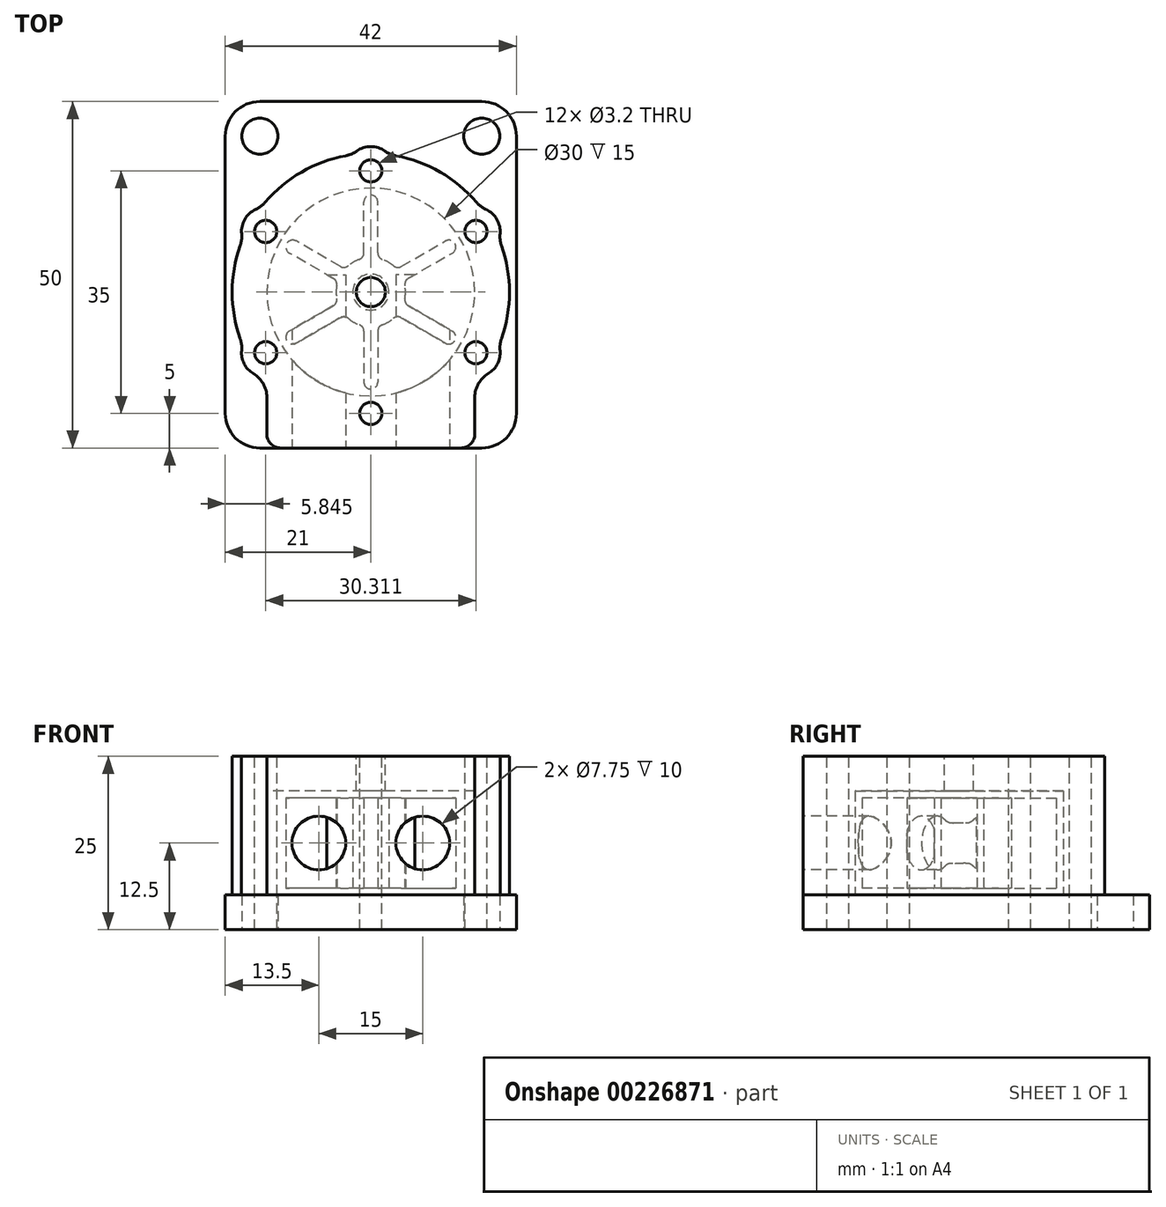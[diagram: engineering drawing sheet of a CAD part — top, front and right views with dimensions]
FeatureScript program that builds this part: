
annotation { "Feature Type Name" : "Feature", "Feature Type Description" : "" }
export const myFeature = defineFeature(function(context is Context, id is Id, definition is map)
    precondition{}
    {
        {
            var Q0;
            Q0=qCreatedBy(makeId("Top.planeOp"),FACE);
            var sketch = newSketch(context, id + "F0", { "sketchPlane" : qUnion([Q0])});
            skLineSegment(sketch, "E0.top", {"start": v(16, 27.5) * mm, "end": v(-16, 27.5) * mm});
            skLineSegment(sketch, "E0.left", {"start": v(21, -17.5) * mm, "end": v(21, 22.5) * mm});
            skLineSegment(sketch, "E0.right", {"start": v(-21, -17.5) * mm, "end": v(-21, 22.5) * mm});
            skPoint(sketch, "E0.middle", {"position": v(0, 0) * mm});
            skPoint(sketch, "E1.visualSharp", {"position": v(-21, 27.5) * mm});
            skArc(sketch, "E1.filletArc", {"start": v(-16, 27.5) * mm, "mid": v(-19.54, 26.04) * mm, "end": v(-21, 22.5) * mm});
            skPoint(sketch, "E2.visualSharp", {"position": v(21, 27.5) * mm});
            skArc(sketch, "E2.filletArc", {"start": v(21, 22.5) * mm, "mid": v(19.54, 26.04) * mm, "end": v(16, 27.5) * mm});
            skCircle(sketch, "E3", {"center": v(-16, 22.5) * mm, "radius": 2.6 * mm});
            skCircle(sketch, "E4", {"center": v(16, 22.5) * mm, "radius": 2.6 * mm});
            skLineSegment(sketch, "E5", {"start": v(-16, -22.5) * mm, "end": v(16, -22.5) * mm});
            skPoint(sketch, "E6.visualSharp", {"position": v(-21, -22.5) * mm});
            skArc(sketch, "E6.filletArc", {"start": v(-21, -17.5) * mm, "mid": v(-19.54, -21.04) * mm, "end": v(-16, -22.5) * mm});
            skPoint(sketch, "E7.visualSharp", {"position": v(21, -22.5) * mm});
            skArc(sketch, "E7.filletArc", {"start": v(16, -22.5) * mm, "mid": v(19.54, -21.04) * mm, "end": v(21, -17.5) * mm});
            skSolve(sketch);
        }
        {
            var Q0;
            Q0 = qSketchRegion(id + "F0", true);
            extrude(context, id + "F1", {"entities" : qUnion([Q0]), "depth" : 5 * mm});
        }
        {
            var Q0;
            Q0=makeQuery(id+"F1.opExtrude","CAP_FACE",FACE,{"disambiguationData":[OSD([sQuery(id+"F0.wireOp",EDGE,"E0.bottom"),sQuery(id+"F0.wireOp",EDGE,"E0.top"),sQuery(id+"F0.wireOp",EDGE,"E0.left"),sQuery(id+"F0.wireOp",EDGE,"E0.right"),sQuery(id+"F0.wireOp",EDGE,"E1.filletArc"),sQuery(id+"F0.wireOp",EDGE,"E2.filletArc"),sQuery(id+"F0.wireOp",EDGE,"c15cc097-3fda-4827-8514-8160edc4b4ba.filletArc"),sQuery(id+"F0.wireOp",EDGE,"696a4059-26aa-422c-bf07-b0a4ac1ae079.filletArc"),sQuery(id+"F0.wireOp",EDGE,"E3"),sQuery(id+"F0.wireOp",EDGE,"E4"),sQuery(id+"F0.wireOp",EDGE,"jZ877vgV-FuZ0-r36g-jPSG-0nmLSFL3s8fu"),sQuery(id+"F0.wireOp",EDGE,"1KYRIAWv-B9v9-mcC8-4xqL-udh9nFA10wgL")])],"isStart":false});
            var sketch = newSketch(context, id + "F2", { "sketchPlane" : qUnion([Q0])});
            skArc(sketch, "E8", {"start": v(18.85, -6.68) * mm, "mid": v(20, 0) * mm, "end": v(18.85, 6.68) * mm});
            skCircle(sketch, "E9", {"center": v(0, 0) * mm, "radius": 15 * mm});
            skLineSegment(sketch, "E10.left", {"start": v(15, -20.5) * mm, "end": v(15, -15.19) * mm});
            skLineSegment(sketch, "E10.right", {"start": v(-15, -20.5) * mm, "end": v(-15, -15.19) * mm});
            skPoint(sketch, "E10.middle", {"position": v(0, -7.67) * mm});
            skPoint(sketch, "E11.orphan", {"position": v(15, 12.15) * mm});
            skPoint(sketch, "E12.trimOffspring.end.orphan", {"position": v(-15, 12.15) * mm});
            skPoint(sketch, "E13.visualSharp", {"position": v(-15, -13.23) * mm});
            skPoint(sketch, "E14.visualSharp", {"position": v(15, -13.23) * mm});
            skLineSegment(sketch, "E15", {"start": v(-13, -22.5) * mm, "end": v(13, -22.5) * mm});
            skPoint(sketch, "E16.visualSharp", {"position": v(-15, -22.5) * mm});
            skArc(sketch, "E16.filletArc", {"start": v(-15, -20.5) * mm, "mid": v(-14.41, -21.91) * mm, "end": v(-13, -22.5) * mm});
            skPoint(sketch, "E17.visualSharp", {"position": v(15, -22.5) * mm});
            skArc(sketch, "E17.filletArc", {"start": v(13, -22.5) * mm, "mid": v(14.41, -21.91) * mm, "end": v(15, -20.5) * mm});
            skCircle(sketch, "E18", {"center": v(0, 0) * mm, "radius": 17.5 * mm, "construction": true});
            skArc(sketch, "E19", {"start": v(2.04, 20.35) * mm, "mid": v(0, 21) * mm, "end": v(-2.04, 20.35) * mm});
            skArc(sketch, "E20.trimOffspring", {"start": v(-3.64, 19.67) * mm, "mid": v(-10, 17.32) * mm, "end": v(-15.21, 12.98) * mm});
            skPoint(sketch, "E21.visualSharp", {"position": v(2.61, 19.83) * mm});
            skArc(sketch, "E21.filletArc", {"start": v(2.04, 20.35) * mm, "mid": v(2.8, 19.92) * mm, "end": v(3.64, 19.67) * mm});
            skPoint(sketch, "E22.visualSharp", {"position": v(-2.61, 19.83) * mm});
            skArc(sketch, "E22.filletArc", {"start": v(-3.64, 19.67) * mm, "mid": v(-2.8, 19.92) * mm, "end": v(-2.04, 20.35) * mm});
            skPoint(sketch, "E23.1.0", {"position": v(-15.87, 12.18) * mm});
            skPoint(sketch, "E23.1.1", {"position": v(-18.48, 7.65) * mm});
            skArc(sketch, "E23.1.2", {"start": v(-16.6, 11.94) * mm, "mid": v(-18.19, 10.5) * mm, "end": v(-18.64, 8.4) * mm});
            skArc(sketch, "E23.1.3", {"start": v(-18.85, 6.68) * mm, "mid": v(-18.65, 7.54) * mm, "end": v(-18.64, 8.4) * mm});
            skArc(sketch, "E23.1.4", {"start": v(-16.6, 11.94) * mm, "mid": v(-15.85, 12.38) * mm, "end": v(-15.21, 12.98) * mm});
            skPoint(sketch, "E23.2.0", {"position": v(-18.48, -7.65) * mm});
            skPoint(sketch, "E23.2.1", {"position": v(-15.87, -12.18) * mm});
            skArc(sketch, "E23.2.2", {"start": v(-18.64, -8.4) * mm, "mid": v(-18.28, -10.33) * mm, "end": v(-16.95, -11.76) * mm});
            skArc(sketch, "E23.2.4", {"start": v(-18.64, -8.4) * mm, "mid": v(-18.65, -7.54) * mm, "end": v(-18.85, -6.68) * mm});
            skPoint(sketch, "E23.3.0", {"position": v(-2.61, -19.83) * mm});
            skPoint(sketch, "E23.3.1", {"position": v(2.61, -19.83) * mm});
            skArc(sketch, "E23.3.2", {"start": v(-2.04, -20.35) * mm, "mid": v(0, -21) * mm, "end": v(2.04, -20.35) * mm});
            skArc(sketch, "E23.3.3", {"start": v(3.64, -19.67) * mm, "mid": v(2.8, -19.92) * mm, "end": v(2.04, -20.35) * mm});
            skArc(sketch, "E23.3.4", {"start": v(-2.04, -20.35) * mm, "mid": v(-2.8, -19.92) * mm, "end": v(-3.64, -19.67) * mm});
            skPoint(sketch, "E23.4.0", {"position": v(15.87, -12.18) * mm});
            skPoint(sketch, "E23.4.1", {"position": v(18.48, -7.65) * mm});
            skArc(sketch, "E23.4.2", {"start": v(16.95, -11.76) * mm, "mid": v(18.28, -10.33) * mm, "end": v(18.64, -8.4) * mm});
            skArc(sketch, "E23.4.3", {"start": v(18.85, -6.68) * mm, "mid": v(18.65, -7.54) * mm, "end": v(18.64, -8.4) * mm});
            skPoint(sketch, "E23.5.0", {"position": v(18.48, 7.65) * mm});
            skPoint(sketch, "E23.5.1", {"position": v(15.87, 12.18) * mm});
            skArc(sketch, "E23.5.2", {"start": v(18.64, 8.4) * mm, "mid": v(18.19, 10.5) * mm, "end": v(16.6, 11.94) * mm});
            skArc(sketch, "E23.5.3", {"start": v(15.21, 12.98) * mm, "mid": v(15.85, 12.38) * mm, "end": v(16.6, 11.94) * mm});
            skArc(sketch, "E23.5.4", {"start": v(18.64, 8.4) * mm, "mid": v(18.65, 7.54) * mm, "end": v(18.85, 6.68) * mm});
            skArc(sketch, "E24.trimOffspring", {"start": v(15.21, 12.98) * mm, "mid": v(10, 17.32) * mm, "end": v(3.64, 19.67) * mm});
            skArc(sketch, "E25.trimOffspring", {"start": v(-18.85, 6.68) * mm, "mid": v(-20, 0) * mm, "end": v(-18.85, -6.68) * mm});
            skPoint(sketch, "E26.newPointA", {"position": v(-16.6, -11.94) * mm});
            skArc(sketch, "E26.filletArc", {"start": v(-15, -15.19) * mm, "mid": v(-15.52, -13.22) * mm, "end": v(-16.95, -11.76) * mm});
            skPoint(sketch, "E27.newPointA", {"position": v(16.6, -11.94) * mm});
            skArc(sketch, "E27.filletArc", {"start": v(16.95, -11.76) * mm, "mid": v(15.52, -13.22) * mm, "end": v(15, -15.19) * mm});
            skSolve(sketch);
        }
        {
            var Q0;
            Q0=makeQuery(id+"F2.imprint","IMPRINT",FACE,{"disambiguationData":[TD([[makeQuery(id+"F2.imprint","IMPRINT",EDGE,{"derivedFrom":sQuery(id+"F2.wireOp",EDGE,"E8")}),1.0]])]});
            extrude(context, id + "F3", {"entities" : qUnion([Q0]), "depth" : 15 * mm});
        }
        {
            var Q0;
            Q0=makeQuery(id+"F3.opExtrude","CAP_FACE",FACE,{"disambiguationData":[OSD([sQuery(id+"F2.wireOp",EDGE,"E8"),sQuery(id+"F2.wireOp",EDGE,"E9"),sQuery(id+"F2.wireOp",EDGE,"E10.left"),sQuery(id+"F2.wireOp",EDGE,"E10.right"),sQuery(id+"F2.wireOp",EDGE,"E13.filletArc"),sQuery(id+"F2.wireOp",EDGE,"E14.filletArc"),sQuery(id+"F2.wireOp",EDGE,"E15"),sQuery(id+"F2.wireOp",EDGE,"E16.filletArc"),sQuery(id+"F2.wireOp",EDGE,"E17.filletArc")])],"isStart":false});
            var sketch = newSketch(context, id + "F4", { "sketchPlane" : qUnion([Q0])});
            skCircle(sketch, "E28", {"center": v(0, 0) * mm, "radius": 17.5 * mm, "construction": true});
            skLineSegment(sketch, "E29", {"start": v(0, 0) * mm, "end": v(0, 17.5) * mm, "construction": true});
            skCircle(sketch, "E30", {"center": v(0, 17.5) * mm, "radius": 1.6 * mm});
            skCircle(sketch, "E31.1.0", {"center": v(-15.16, 8.75) * mm, "radius": 1.6 * mm});
            skCircle(sketch, "E31.2.0", {"center": v(-15.16, -8.75) * mm, "radius": 1.6 * mm});
            skCircle(sketch, "E31.3.0", {"center": v(0, -17.5) * mm, "radius": 1.6 * mm});
            skCircle(sketch, "E31.4.0", {"center": v(15.16, -8.75) * mm, "radius": 1.6 * mm});
            skCircle(sketch, "E31.5.0", {"center": v(15.16, 8.75) * mm, "radius": 1.6 * mm});
            skLineSegment(sketch, "E32", {"start": v(-11, -18.5) * mm, "end": v(11, -18.5) * mm, "construction": true});
            skSolve(sketch);
        }
        {
            var Q0;
            Q0 = qSketchRegion(id + "F4", true);
            extrude(context, id + "F5", {"entities" : qUnion([Q0]), "operationType" : NewBodyOperationType.REMOVE, "oppositeDirection" : true, "depth" : 25 * mm});
        }
        {
            var Q0;
            Q0=makeQuery(id+"F3.opExtrude","CAP_FACE",FACE,{"disambiguationData":[OSD([sQuery(id+"F2.wireOp",EDGE,"E8"),sQuery(id+"F2.wireOp",EDGE,"E9"),sQuery(id+"F2.wireOp",EDGE,"E10.left"),sQuery(id+"F2.wireOp",EDGE,"E10.right"),sQuery(id+"F2.wireOp",EDGE,"E13.filletArc"),sQuery(id+"F2.wireOp",EDGE,"E14.filletArc"),sQuery(id+"F2.wireOp",EDGE,"E15"),sQuery(id+"F2.wireOp",EDGE,"E16.filletArc"),sQuery(id+"F2.wireOp",EDGE,"E17.filletArc")])],"isStart":false});
            var sketch = newSketch(context, id + "F6", { "sketchPlane" : qUnion([Q0])});
            skCircle(sketch, "E33.0", {"center": v(0, 0) * mm, "radius": 15 * mm, "construction": true});
            skCircle(sketch, "E34.0", {"center": v(0, 17.5) * mm, "radius": 1.6 * mm, "construction": true});
            skCircle(sketch, "E35.0", {"center": v(15.16, 8.75) * mm, "radius": 1.6 * mm, "construction": true});
            skCircle(sketch, "E36.0", {"center": v(15.16, -8.75) * mm, "radius": 1.6 * mm, "construction": true});
            skCircle(sketch, "E37.0", {"center": v(-15.16, -8.75) * mm, "radius": 1.6 * mm, "construction": true});
            skCircle(sketch, "E38.0", {"center": v(-15.16, 8.75) * mm, "radius": 1.6 * mm, "construction": true});
            skLineSegment(sketch, "E39.0.0", {"start": v(-15, -15.19) * mm, "end": v(-15, -20.5) * mm});
            skArc(sketch, "E39.0.1", {"start": v(-15, -20.5) * mm, "mid": v(-14.41, -21.91) * mm, "end": v(-13, -22.5) * mm});
            skLineSegment(sketch, "E39.0.2", {"start": v(-13, -22.5) * mm, "end": v(13, -22.5) * mm});
            skArc(sketch, "E39.0.3", {"start": v(13, -22.5) * mm, "mid": v(14.41, -21.91) * mm, "end": v(15, -20.5) * mm});
            skLineSegment(sketch, "E39.0.4", {"start": v(15, -20.5) * mm, "end": v(15, -15.19) * mm});
            skArc(sketch, "E39.0.5", {"start": v(15, -15.19) * mm, "mid": v(15.52, -13.22) * mm, "end": v(16.95, -11.76) * mm});
            skArc(sketch, "E39.0.6", {"start": v(16.95, -11.76) * mm, "mid": v(18.28, -10.33) * mm, "end": v(18.64, -8.4) * mm});
            skArc(sketch, "E39.0.7", {"start": v(18.64, -8.4) * mm, "mid": v(18.65, -7.54) * mm, "end": v(18.85, -6.68) * mm});
            skArc(sketch, "E39.0.8", {"start": v(18.85, -6.68) * mm, "mid": v(20, 0) * mm, "end": v(18.85, 6.68) * mm});
            skArc(sketch, "E39.0.9", {"start": v(18.85, 6.68) * mm, "mid": v(18.65, 7.54) * mm, "end": v(18.64, 8.4) * mm});
            skArc(sketch, "E39.0.10", {"start": v(18.64, 8.4) * mm, "mid": v(18.19, 10.5) * mm, "end": v(16.6, 11.94) * mm});
            skArc(sketch, "E39.0.11", {"start": v(16.6, 11.94) * mm, "mid": v(15.85, 12.38) * mm, "end": v(15.21, 12.98) * mm});
            skArc(sketch, "E39.0.12", {"start": v(15.21, 12.98) * mm, "mid": v(10, 17.32) * mm, "end": v(3.64, 19.67) * mm});
            skArc(sketch, "E39.0.13", {"start": v(3.64, 19.67) * mm, "mid": v(2.8, 19.92) * mm, "end": v(2.04, 20.35) * mm});
            skArc(sketch, "E39.0.14", {"start": v(2.04, 20.35) * mm, "mid": v(0, 21) * mm, "end": v(-2.04, 20.35) * mm});
            skArc(sketch, "E39.0.15", {"start": v(-2.04, 20.35) * mm, "mid": v(-2.8, 19.92) * mm, "end": v(-3.64, 19.67) * mm});
            skArc(sketch, "E39.0.16", {"start": v(-3.64, 19.67) * mm, "mid": v(-10, 17.32) * mm, "end": v(-15.21, 12.98) * mm});
            skArc(sketch, "E39.0.17", {"start": v(-15.21, 12.98) * mm, "mid": v(-15.85, 12.38) * mm, "end": v(-16.6, 11.94) * mm});
            skArc(sketch, "E39.0.18", {"start": v(-16.6, 11.94) * mm, "mid": v(-18.19, 10.5) * mm, "end": v(-18.64, 8.4) * mm});
            skArc(sketch, "E39.0.19", {"start": v(-18.64, 8.4) * mm, "mid": v(-18.65, 7.54) * mm, "end": v(-18.85, 6.68) * mm});
            skArc(sketch, "E39.0.20", {"start": v(-18.85, 6.68) * mm, "mid": v(-20, 0) * mm, "end": v(-18.85, -6.68) * mm});
            skArc(sketch, "E39.0.21", {"start": v(-18.85, -6.68) * mm, "mid": v(-18.65, -7.54) * mm, "end": v(-18.64, -8.4) * mm});
            skArc(sketch, "E39.0.22", {"start": v(-18.64, -8.4) * mm, "mid": v(-18.28, -10.33) * mm, "end": v(-16.95, -11.76) * mm});
            skArc(sketch, "E39.0.23", {"start": v(-16.95, -11.76) * mm, "mid": v(-15.52, -13.22) * mm, "end": v(-15, -15.19) * mm});
            skSolve(sketch);
        }
        {
            var Q0;
            Q0=makeQuery(id+"F6.imprint","IMPRINT",FACE,{"disambiguationData":[TD([[makeQuery(id+"F6.imprint","IMPRINT",EDGE,{"derivedFrom":sQuery(id+"F6.wireOp",EDGE,"4ad2e2d8-0146-45ca-a098-c5cb41a828be.0.0")}),1.0]])]});
            var Q1;
            Q1=makeQuery(id+"F4.imprint","IMPRINT",FACE,{"disambiguationData":[TD([[makeQuery(id+"F4.imprint","IMPRINT",EDGE,{"derivedFrom":sQuery(id+"F4.wireOp",EDGE,"E30")}),-1.0]])]});
            extrude(context, id + "F7", {"entities" : qUnion([Q0, Q1]), "depth" : 5 * mm});
        }
        {
            var Q0;
            Q0=makeQuery(id+"F6.imprint","IMPRINT",FACE,{"disambiguationData":[TD([[makeQuery(id+"F6.imprint","IMPRINT",EDGE,{"derivedFrom":makeQuery(id+"F3.opExtrude","CAP_EDGE",EDGE,{"disambiguationData":[OSD([sQuery(id+"F2.wireOp",EDGE,"E9")])],"isStart":false})}),1.0]])]});
            extrude(context, id + "F8", {"entities" : qUnion([Q0]), "operationType" : NewBodyOperationType.ADD, "depth" : 5 * mm});
        }
        {
            var Q0;
            Q0=qCreatedBy(makeId("Top.planeOp"),FACE);
            var sketch = newSketch(context, id + "F9", { "sketchPlane" : qUnion([Q0])});
            skCircle(sketch, "E40", {"center": v(0, -17.5) * mm, "radius": 1.1 * mm});
            skCircle(sketch, "E41.1.0", {"center": v(15.16, -8.75) * mm, "radius": 1.1 * mm});
            skCircle(sketch, "E41.2.0", {"center": v(15.16, 8.75) * mm, "radius": 1.1 * mm});
            skCircle(sketch, "E41.3.0", {"center": v(0, 17.5) * mm, "radius": 1.1 * mm});
            skCircle(sketch, "E41.4.0", {"center": v(-15.16, 8.75) * mm, "radius": 1.1 * mm});
            skCircle(sketch, "E41.5.0", {"center": v(-15.16, -8.75) * mm, "radius": 1.1 * mm});
            skPoint(sketch, "E41.center", {"position": v(0, 0) * mm});
            skSolve(sketch);
        }
        {
            var Q0;
            Q0 = qSketchRegion(id + "F9", true);
            extrude(context, id + "F10", {"entities" : qUnion([Q0]), "operationType" : NewBodyOperationType.REMOVE, "depth" : 25 * mm});
        }
        {
            var Q0;
            {var subQ0=sQuery(id+"F2.wireOp",EDGE,"E9");Q0=makeQuery(id+"F8.boolean.opBoolean","MERGE",FACE,{"derivedFrom":[makeQuery(id+"F7.opExtrude","CAP_FACE",FACE,{"disambiguationData":[OSD([subQ0,sQuery(id+"F4.wireOp",EDGE,"E30"),sQuery(id+"F4.wireOp",EDGE,"E31.1.0"),sQuery(id+"F4.wireOp",EDGE,"E31.2.0"),sQuery(id+"F4.wireOp",EDGE,"E31.3.0"),sQuery(id+"F4.wireOp",EDGE,"E31.4.0"),sQuery(id+"F4.wireOp",EDGE,"E31.5.0"),sQuery(id+"F4.wireOp",EDGE,"KjSmSesU-TgWE-n0Dj-QpoN-ZwIoElxS9IT5"),sQuery(id+"F4.wireOp",EDGE,"5PmntXCd-CVhU-zGXc-Cbz9-EEJ1zOj0CbWe"),sQuery(id+"F6.wireOp",EDGE,"4ad2e2d8-0146-45ca-a098-c5cb41a828be.0.0"),sQuery(id+"F6.wireOp",EDGE,"4ad2e2d8-0146-45ca-a098-c5cb41a828be.0.1"),sQuery(id+"F6.wireOp",EDGE,"4ad2e2d8-0146-45ca-a098-c5cb41a828be.0.2"),sQuery(id+"F6.wireOp",EDGE,"4ad2e2d8-0146-45ca-a098-c5cb41a828be.0.3"),sQuery(id+"F6.wireOp",EDGE,"4ad2e2d8-0146-45ca-a098-c5cb41a828be.0.4"),sQuery(id+"F6.wireOp",EDGE,"4ad2e2d8-0146-45ca-a098-c5cb41a828be.0.5"),sQuery(id+"F6.wireOp",EDGE,"4ad2e2d8-0146-45ca-a098-c5cb41a828be.0.6"),sQuery(id+"F6.wireOp",EDGE,"4ad2e2d8-0146-45ca-a098-c5cb41a828be.0.7")])],"isStart":false}),makeQuery(id+"F8.opExtrude","CAP_FACE",FACE,{"disambiguationData":[OSD([subQ0])],"isStart":false})]});}
            var sketch = newSketch(context, id + "F11", { "sketchPlane" : qUnion([Q0])});
            skCircle(sketch, "E42", {"center": v(0, 0) * mm, "radius": 2.1 * mm});
            skSolve(sketch);
        }
        {
            var Q0;
            Q0 = qSketchRegion(id + "F11", true);
            extrude(context, id + "F12", {"entities" : qUnion([Q0]), "operationType" : NewBodyOperationType.REMOVE, "oppositeDirection" : true, "depth" : 10 * mm});
        }
        {
            var Q0;
            Q0=makeQuery(id+"F1.opExtrude","CAP_FACE",FACE,{"disambiguationData":[OSD([sQuery(id+"F0.wireOp",EDGE,"E0.bottom"),sQuery(id+"F0.wireOp",EDGE,"E0.top"),sQuery(id+"F0.wireOp",EDGE,"E0.left"),sQuery(id+"F0.wireOp",EDGE,"E0.right"),sQuery(id+"F0.wireOp",EDGE,"E1.filletArc"),sQuery(id+"F0.wireOp",EDGE,"E2.filletArc"),sQuery(id+"F0.wireOp",EDGE,"c15cc097-3fda-4827-8514-8160edc4b4ba.filletArc"),sQuery(id+"F0.wireOp",EDGE,"696a4059-26aa-422c-bf07-b0a4ac1ae079.filletArc"),sQuery(id+"F0.wireOp",EDGE,"E3"),sQuery(id+"F0.wireOp",EDGE,"E4")])],"isStart":true});
            var sketch = newSketch(context, id + "F13", { "sketchPlane" : qUnion([Q0])});
            skCircle(sketch, "E43", {"center": v(0, 0) * mm, "radius": 2.1 * mm});
            skSolve(sketch);
        }
        {
            var Q0;
            Q0=qCreatedBy(makeId("Top.planeOp"),FACE);
            cPlane(context, id + "F14", {"entities" : qUnion([Q0]), "cplaneType" : CPlaneType.OFFSET, "offset" : 6 * mm, "width" : 150 * mm, "height" : 150 * mm});
        }
        {
            var Q0;
            Q0=qCreatedBy(id+"F14.planeOp",FACE);
            var sketch = newSketch(context, id + "F15", { "sketchPlane" : qUnion([Q0])});
            skCircle(sketch, "E44", {"center": v(0, 0) * mm, "radius": 2.6 * mm});
            skArc(sketch, "E45", {"start": v(-1.67, 4.71) * mm, "mid": v(-2.5, 4.33) * mm, "end": v(-3.25, 3.8) * mm});
            skLineSegment(sketch, "E46", {"start": v(0, 0) * mm, "end": v(0, 13) * mm});
            skArc(sketch, "E47.0.endCap", {"start": v(-1, 13) * mm, "mid": v(0, 14) * mm, "end": v(1, 13) * mm});
            skLineSegment(sketch, "E47.0.left", {"start": v(-1, 5.66) * mm, "end": v(-1, 13) * mm});
            skLineSegment(sketch, "E47.0.right", {"start": v(1, 5.66) * mm, "end": v(1, 13) * mm});
            skPoint(sketch, "E48.visualSharp", {"position": v(1, 4.9) * mm});
            skArc(sketch, "E48.filletArc", {"start": v(1, 5.66) * mm, "mid": v(1.18, 5.08) * mm, "end": v(1.67, 4.71) * mm});
            skPoint(sketch, "E49.visualSharp", {"position": v(-1, 4.9) * mm});
            skArc(sketch, "E49.filletArc", {"start": v(-1.67, 4.71) * mm, "mid": v(-1.18, 5.08) * mm, "end": v(-1, 5.66) * mm});
            skLineSegment(sketch, "E50.1.0", {"start": v(-4.4, 3.7) * mm, "end": v(-10.76, 7.37) * mm});
            skArc(sketch, "E50.1.1", {"start": v(-11.76, 5.63) * mm, "mid": v(-12.12, 7) * mm, "end": v(-10.76, 7.37) * mm});
            skLineSegment(sketch, "E50.1.2", {"start": v(-5.4, 1.96) * mm, "end": v(-11.76, 5.63) * mm});
            skPoint(sketch, "E50.1.3", {"position": v(-4.74, 1.58) * mm});
            skPoint(sketch, "E50.1.4", {"position": v(-3.74, 3.32) * mm});
            skArc(sketch, "E50.1.5", {"start": v(-4.92, 0.91) * mm, "mid": v(-5, 1.51) * mm, "end": v(-5.4, 1.96) * mm});
            skArc(sketch, "E50.1.6", {"start": v(-4.4, 3.7) * mm, "mid": v(-3.8, 3.56) * mm, "end": v(-3.25, 3.8) * mm});
            skLineSegment(sketch, "E50.2.0", {"start": v(-5.4, -1.96) * mm, "end": v(-11.76, -5.63) * mm});
            skArc(sketch, "E50.2.1", {"start": v(-10.76, -7.37) * mm, "mid": v(-12.12, -7) * mm, "end": v(-11.76, -5.63) * mm});
            skLineSegment(sketch, "E50.2.2", {"start": v(-4.4, -3.7) * mm, "end": v(-10.76, -7.37) * mm});
            skPoint(sketch, "E50.2.3", {"position": v(-3.74, -3.32) * mm});
            skPoint(sketch, "E50.2.4", {"position": v(-4.74, -1.58) * mm});
            skArc(sketch, "E50.2.5", {"start": v(-3.25, -3.8) * mm, "mid": v(-3.8, -3.56) * mm, "end": v(-4.4, -3.7) * mm});
            skArc(sketch, "E50.2.6", {"start": v(-5.4, -1.96) * mm, "mid": v(-5, -1.51) * mm, "end": v(-4.92, -0.91) * mm});
            skLineSegment(sketch, "E50.3.0", {"start": v(-1, -5.66) * mm, "end": v(-1, -13) * mm});
            skArc(sketch, "E50.3.1", {"start": v(1, -13) * mm, "mid": v(0, -14) * mm, "end": v(-1, -13) * mm});
            skLineSegment(sketch, "E50.3.2", {"start": v(1, -5.66) * mm, "end": v(1, -13) * mm});
            skPoint(sketch, "E50.3.3", {"position": v(1, -4.9) * mm});
            skPoint(sketch, "E50.3.4", {"position": v(-1, -4.9) * mm});
            skArc(sketch, "E50.3.5", {"start": v(1.67, -4.71) * mm, "mid": v(1.18, -5.08) * mm, "end": v(1, -5.66) * mm});
            skArc(sketch, "E50.3.6", {"start": v(-1, -5.66) * mm, "mid": v(-1.18, -5.08) * mm, "end": v(-1.67, -4.71) * mm});
            skLineSegment(sketch, "E50.4.0", {"start": v(4.4, -3.7) * mm, "end": v(10.76, -7.37) * mm});
            skArc(sketch, "E50.4.1", {"start": v(11.76, -5.63) * mm, "mid": v(12.12, -7) * mm, "end": v(10.76, -7.37) * mm});
            skLineSegment(sketch, "E50.4.2", {"start": v(5.4, -1.96) * mm, "end": v(11.76, -5.63) * mm});
            skPoint(sketch, "E50.4.3", {"position": v(4.74, -1.58) * mm});
            skPoint(sketch, "E50.4.4", {"position": v(3.74, -3.32) * mm});
            skArc(sketch, "E50.4.5", {"start": v(4.92, -0.91) * mm, "mid": v(5, -1.51) * mm, "end": v(5.4, -1.96) * mm});
            skArc(sketch, "E50.4.6", {"start": v(4.4, -3.7) * mm, "mid": v(3.8, -3.56) * mm, "end": v(3.25, -3.8) * mm});
            skLineSegment(sketch, "E50.5.0", {"start": v(5.4, 1.96) * mm, "end": v(11.76, 5.63) * mm});
            skArc(sketch, "E50.5.1", {"start": v(10.76, 7.37) * mm, "mid": v(12.12, 7) * mm, "end": v(11.76, 5.63) * mm});
            skLineSegment(sketch, "E50.5.2", {"start": v(4.4, 3.7) * mm, "end": v(10.76, 7.37) * mm});
            skPoint(sketch, "E50.5.3", {"position": v(3.74, 3.32) * mm});
            skPoint(sketch, "E50.5.4", {"position": v(4.74, 1.58) * mm});
            skArc(sketch, "E50.5.5", {"start": v(3.25, 3.8) * mm, "mid": v(3.8, 3.56) * mm, "end": v(4.4, 3.7) * mm});
            skArc(sketch, "E50.5.6", {"start": v(5.4, 1.96) * mm, "mid": v(5, 1.51) * mm, "end": v(4.92, 0.91) * mm});
            skArc(sketch, "E51.trimOffspring", {"start": v(3.25, 3.8) * mm, "mid": v(2.5, 4.33) * mm, "end": v(1.67, 4.71) * mm});
            skArc(sketch, "E52.trimOffspring", {"start": v(4.92, -0.91) * mm, "mid": v(5, 0) * mm, "end": v(4.92, 0.91) * mm});
            skArc(sketch, "E53.trimOffspring", {"start": v(1.67, -4.71) * mm, "mid": v(2.5, -4.33) * mm, "end": v(3.25, -3.8) * mm});
            skArc(sketch, "E54.trimOffspring", {"start": v(-3.25, -3.8) * mm, "mid": v(-2.5, -4.33) * mm, "end": v(-1.67, -4.71) * mm});
            skArc(sketch, "E55.trimOffspring", {"start": v(-4.92, 0.91) * mm, "mid": v(-5, 0) * mm, "end": v(-4.92, -0.91) * mm});
            skSolve(sketch);
        }
        {
            var Q0;
            Q0 = qSketchRegion(id + "F15", true);
            extrude(context, id + "F16", {"entities" : qUnion([Q0]), "depth" : 13 * mm});
        }
        {
            var Q0;
            Q0=makeQuery(id+"F3.opExtrude","SWEPT_FACE",FACE,{"disambiguationData":[OSD([sQuery(id+"F2.wireOp",EDGE,"E15")])]});
            var sketch = newSketch(context, id + "F17", { "sketchPlane" : qUnion([Q0])});
            skLineSegment(sketch, "E56", {"start": v(-13, 12.5) * mm, "end": v(13, 12.5) * mm, "construction": true});
            skCircle(sketch, "E57", {"center": v(-7.5, 12.5) * mm, "radius": 3.88 * mm});
            skCircle(sketch, "E58", {"center": v(7.5, 12.5) * mm, "radius": 3.88 * mm});
            skSolve(sketch);
        }
        {
            var Q0;
            Q0 = qSketchRegion(id + "F17", true);
            extrude(context, id + "F18", {"entities" : qUnion([Q0]), "operationType" : NewBodyOperationType.REMOVE, "oppositeDirection" : true, "depth" : 25 * mm});
        }
    });
